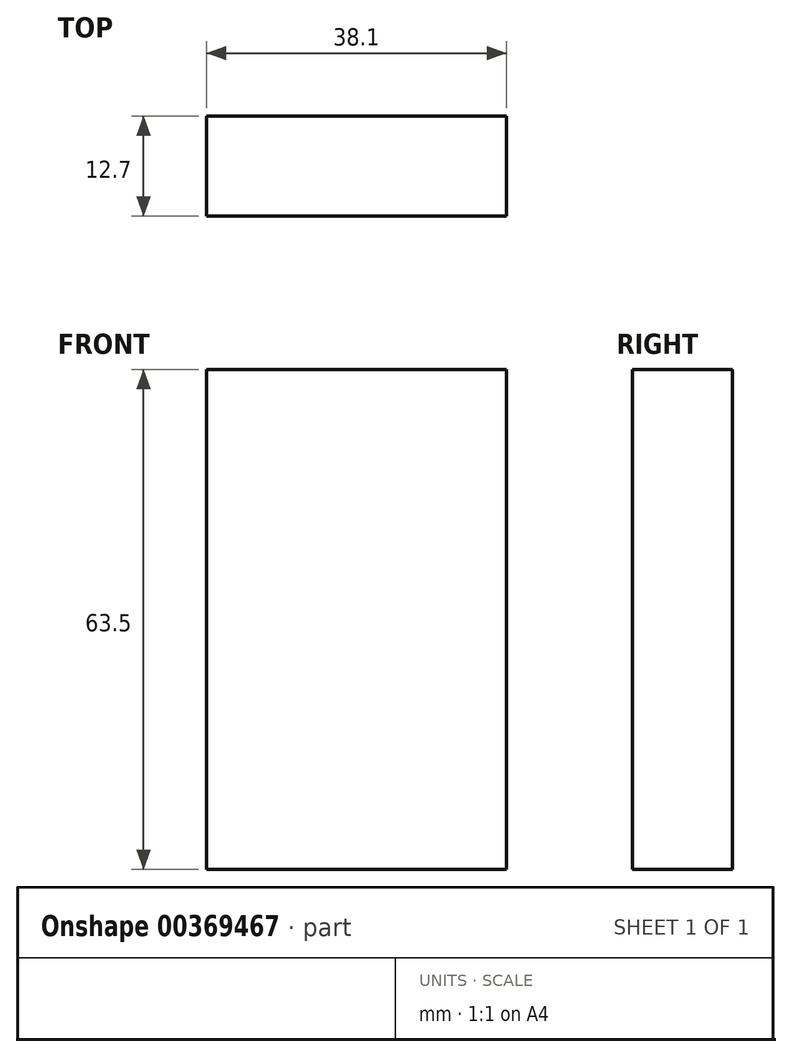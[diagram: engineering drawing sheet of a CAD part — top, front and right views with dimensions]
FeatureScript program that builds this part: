
annotation { "Feature Type Name" : "Feature", "Feature Type Description" : "" }
export const myFeature = defineFeature(function(context is Context, id is Id, definition is map)
    precondition{}
    {
        {
            var Q0;
            Q0=qCreatedBy(makeId("Front.planeOp"),FACE);
            var sketch = newSketch(context, id + "F0", { "sketchPlane" : qUnion([Q0])});
            skLineSegment(sketch, "E0.bottom", {"start": v(0, 0) * mm, "end": v(38.1, 0) * mm});
            skLineSegment(sketch, "E0.top", {"start": v(0, 63.5) * mm, "end": v(38.1, 63.5) * mm});
            skLineSegment(sketch, "E0.left", {"start": v(0, 0) * mm, "end": v(0, 63.5) * mm});
            skLineSegment(sketch, "E0.right", {"start": v(38.1, 0) * mm, "end": v(38.1, 63.5) * mm});
            skSolve(sketch);
        }
        {
            var Q0;
            Q0 = qSketchRegion(id + "F0", true);
            extrude(context, id + "F1", {"entities" : qUnion([Q0]), "depth" : 12.7 * mm});
        }
    });
